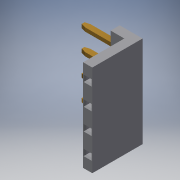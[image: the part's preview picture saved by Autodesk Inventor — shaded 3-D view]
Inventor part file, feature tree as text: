
AUTODESK INVENTOR PART (.ipt)
format: ipt  version: 2018.3 (Build 223284000, 284)  size: 211,456 bytes
history: native  units: mm
features: chamfer x12, extrude x4, sketch x4
ambient origin geometry x8: Origin, YZ Plane, XZ Plane, XY Plane, X Axis, Y Axis, Z Axis, Center Point
bodies: Body1 (feature_tree)
feature tree (20):
  extrude  "Extrusion4"  Depth=1.0mm
  extrude  "Extrusion5"  Depth=1.0mm
  extrude  "Extrusion6"  Depth=3.5mm TaperAngle=0.0deg
  chamfer  "Chamfer5"  Distance=0.6mm
  chamfer  "Chamfer6"  Distance=0.4mm
  chamfer  "Chamfer7"  Distance=0.6mm
  chamfer  "Chamfer8"  Distance=0.4mm
  chamfer  "Chamfer9"  Distance=0.2mm
  chamfer  "Chamfer10"  Distance=0.2mm
  chamfer  "Chamfer11"  Distance=0.2mm
  chamfer  "Chamfer12"  Distance=3.5mm
  extrude  "Extrusion7"  Depth=1.29mm
  chamfer  "Chamfer13"  Distance=1.94mm
  chamfer  "Chamfer14"  Distance=0.4mm
  chamfer  "Chamfer15"  Distance=1.94mm
  chamfer  "Chamfer16"  Distance=1.29mm
  sketch  "Sketch4"  dims[d22=1.5mm d23=1.0mm]
  sketch  "Sketch5"  dims[d24=1.0mm d25=2.0mm]
  sketch  "Sketch6"  dims[d26=10.0mm d27=0.0mm d28=3.5mm d29=0.0mm]
  sketch  "Sketch7"  dims[d30=0.4mm d31=0.6mm d32=0.4mm d33=0.6mm d36=0.4mm d37=0.6mm d38=1.94mm d40=0.2mm d41=0.2mm d42=0.2mm d47=3.5mm d48=0.0mm d49=1.29mm d50=1.94mm d51=0.4mm d52=0.6mm d53=0.2mm d54=1.94mm d55=1.29mm d56=0.15mm d57=0.5mm d58=45.0deg d59=0.15mm d60=0.5mm d61=45.0deg d62=0.15mm d63=0.5mm d64=45.0deg d65=0.15mm d66=0.5mm d67=45.0deg d68=0.15mm d69=0.5mm d70=45.0deg d71=0.15mm d72=0.5mm d73=45.0deg d74=0.15mm d75=0.5mm d76=45.0deg d77=0.15mm d78=0.5mm d79=45.0deg d80=0.2mm d81=0.6mm d82=0.4mm d83=0.4mm d84=0.4mm d85=0.4mm d86=0.2mm d87=3.7mm d88=0.0mm d89=0.15mm d90=0.5mm d91=45.0deg d92=0.15mm d93=0.5mm d94=45.0deg d95=0.15mm d96=0.5mm d97=45.0deg d98=0.15mm d99=0.5mm d100=45.0deg]
